# Revit family: Door_Overhead-Sectional_CarriageHouseDC_Belize
name_source: partatom
category: Doors
units: mm (PartAtom-declared; Revit-internal decimal feet)

## family parameters
Always vertical = Yes
Classification Number = 23.30.10.17.37.14
Cut with Voids When Loaded = No
Host = Wall
Room Calculation Point = No
Shared = No

## types (1)
- Design as Specified
    Assembly Code = B2030410
    Available Options = [Paint Grade][Stain Grade], [Ogee Trim Edge][Eased Trim Edge][Square Trim Edge]
    Description = Carriage House Wood Overhead Sectional Door - Belize as Specified
    Door Panel Design = Door_Overhead-Sectional-Panel_CarriageHouseDC_Belize : Design as Specified
    Expected Lifespan (Years) = 0
    Fire Rating = As Specified in 08360
    Function = Exterior
    Keynote = 08360
    Maintenance Schedule (Months) = 0
    Manufacturer = Carriage House Door Company
    Manufacturer Fax = 916-375-8874
    Manufacturer Website = http://www.carriagedoor.com
    Model = Design as Specified
    Product Data = http://www.arcat.com
    Product Properties = http://www.carriagedoor.com
    R-Value = 0
    RO Offset = 0' - 0"
    Revision = R1_2015-10
    Rough Height = 0' - 0"
    Rough Width = 0' - 0"
    Sales Information = http://www.carriagedoor.com
    Standards Conformance = Possible WUI Fire Code Compliance  ;  SFM 12-7A-1
    Thickness = 0' - 0"
    URL = http://www.carriagedoor.com
    Wall Closure = By host
    Warranty Duration (Years) = 0

## geometry (parser evidence)
native form markers: Blend x8, Sweep x13
no freeform markers — native parametric forms only
